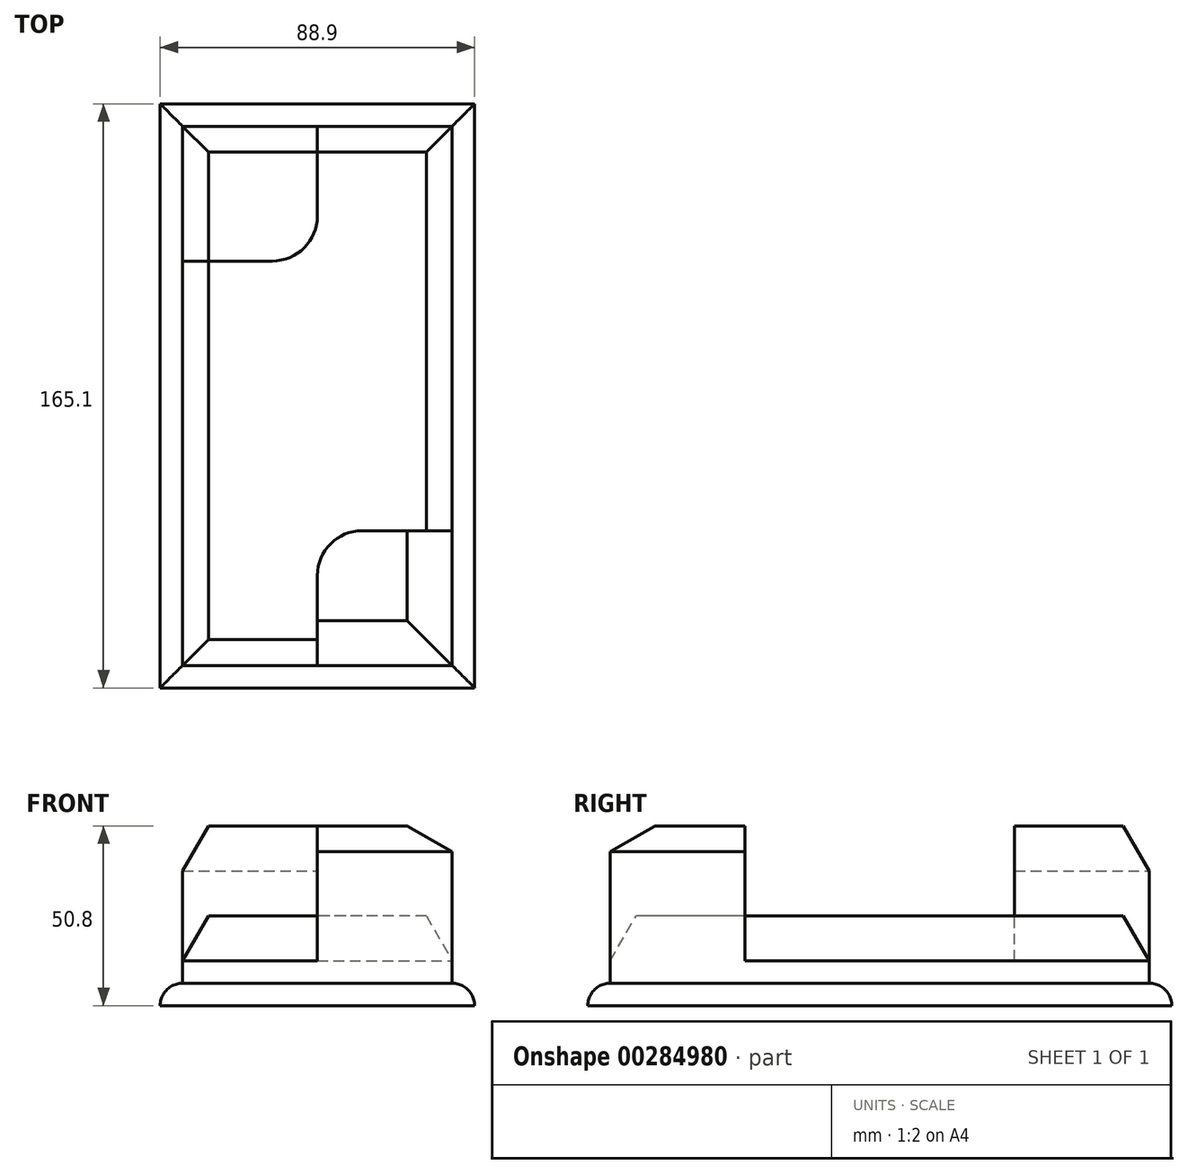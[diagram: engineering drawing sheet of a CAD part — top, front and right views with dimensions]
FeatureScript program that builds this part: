
annotation { "Feature Type Name" : "Feature", "Feature Type Description" : "" }
export const myFeature = defineFeature(function(context is Context, id is Id, definition is map)
    precondition{}
    {
        {
            var Q0;
            Q0=qCreatedBy(makeId("Top.planeOp"),FACE);
            var sketch = newSketch(context, id + "F0", { "sketchPlane" : qUnion([Q0])});
            skLineSegment(sketch, "E0.bottom", {"start": v(38.1, 76.2) * mm, "end": v(-38.1, 76.2) * mm});
            skLineSegment(sketch, "E0.top", {"start": v(38.1, -76.2) * mm, "end": v(-38.1, -76.2) * mm});
            skLineSegment(sketch, "E0.left", {"start": v(38.1, 76.2) * mm, "end": v(38.1, -76.2) * mm});
            skLineSegment(sketch, "E0.right", {"start": v(-38.1, 76.2) * mm, "end": v(-38.1, -76.2) * mm});
            skPoint(sketch, "E0.middle", {"position": v(0, 0) * mm});
            skLineSegment(sketch, "E1.0", {"start": v(44.45, 82.55) * mm, "end": v(-44.45, 82.55) * mm});
            skLineSegment(sketch, "E1.1", {"start": v(44.45, 82.55) * mm, "end": v(44.45, -82.55) * mm});
            skLineSegment(sketch, "E1.2", {"start": v(44.45, -82.55) * mm, "end": v(-44.45, -82.55) * mm});
            skLineSegment(sketch, "E1.3", {"start": v(-44.45, 82.55) * mm, "end": v(-44.45, -82.55) * mm});
            skPoint(sketch, "E2", {"position": v(0, 76.2) * mm});
            skPoint(sketch, "E3", {"position": v(-38.1, 38.1) * mm});
            skLineSegment(sketch, "E4", {"start": v(-38.1, 38.1) * mm, "end": v(-12.7, 38.1) * mm});
            skLineSegment(sketch, "E5", {"start": v(0, 50.8) * mm, "end": v(0, 76.2) * mm});
            skPoint(sketch, "E6.visualSharp", {"position": v(0, 38.1) * mm});
            skArc(sketch, "E6.filletArc", {"start": v(-12.7, 38.1) * mm, "mid": v(-3.72, 41.82) * mm, "end": v(0, 50.8) * mm});
            skPoint(sketch, "E7", {"position": v(38.1, -38.1) * mm});
            skLineSegment(sketch, "E8", {"start": v(38.1, -38.1) * mm, "end": v(38.1, -38.1) * mm});
            skLineSegment(sketch, "E9", {"start": v(0, -76.2) * mm, "end": v(0, -50.8) * mm});
            skLineSegment(sketch, "E10", {"start": v(12.7, -38.1) * mm, "end": v(38.1, -38.1) * mm});
            skPoint(sketch, "E11.visualSharp", {"position": v(0, -38.1) * mm});
            skArc(sketch, "E11.filletArc", {"start": v(12.7, -38.1) * mm, "mid": v(3.72, -41.82) * mm, "end": v(0, -50.8) * mm});
            skSolve(sketch);
        }
        {
            var Q0;
            Q0=makeQuery(id+"F0.imprint","IMPRINT",FACE,{"disambiguationData":[TD([[makeQuery(id+"F0.imprint","IMPRINT",EDGE,{"derivedFrom":sQuery(id+"F0.wireOp",EDGE,"E1.0")}),1.0]])]});
            var Q1;
            {var subQ1=sQuery(id+"F0.wireOp",EDGE,"E4");Q1=makeQuery(id+"F0.imprint","IMPRINT",FACE,{"disambiguationData":[TD([[makeQuery(id+"F0.imprint","IMPRINT",EDGE,{"derivedFrom":subQ1}),1.0]])]});}
            var Q2;
            {var subQ3=sQuery(id+"F0.wireOp",EDGE,"E4");Q2=makeQuery(id+"F0.imprint","IMPRINT",FACE,{"disambiguationData":[TD([[makeQuery(id+"F0.imprint","IMPRINT",EDGE,{"derivedFrom":subQ3}),-1.0]])]});}
            var Q3;
            {var subQ4=sQuery(id+"F0.wireOp",EDGE,"E9");Q3=makeQuery(id+"F0.imprint","IMPRINT",FACE,{"disambiguationData":[TD([[makeQuery(id+"F0.imprint","IMPRINT",EDGE,{"derivedFrom":subQ4}),-1.0]])]});}
            extrude(context, id + "F1", {"entities" : qUnion([Q0, Q1, Q2, Q3]), "depth" : 6.35 * mm});
        }
        {
            var Q0;
            {var subQ3=sQuery(id+"F0.wireOp",EDGE,"E4");Q0=makeQuery(id+"F0.imprint","IMPRINT",FACE,{"disambiguationData":[TD([[makeQuery(id+"F0.imprint","IMPRINT",EDGE,{"derivedFrom":subQ3}),-1.0]])]});}
            var Q1;
            {var subQ1=sQuery(id+"F0.wireOp",EDGE,"E4");Q1=makeQuery(id+"F0.imprint","IMPRINT",FACE,{"disambiguationData":[TD([[makeQuery(id+"F0.imprint","IMPRINT",EDGE,{"derivedFrom":subQ1}),1.0]])]});}
            var Q2;
            {var subQ4=sQuery(id+"F0.wireOp",EDGE,"E9");Q2=makeQuery(id+"F0.imprint","IMPRINT",FACE,{"disambiguationData":[TD([[makeQuery(id+"F0.imprint","IMPRINT",EDGE,{"derivedFrom":subQ4}),-1.0]])]});}
            extrude(context, id + "F2", {"entities" : qUnion([Q0, Q1, Q2]), "operationType" : NewBodyOperationType.ADD, "depth" : 25.4 * mm});
        }
        {
            var Q0;
            {var subQ1=sQuery(id+"F0.wireOp",EDGE,"E4");Q0=makeQuery(id+"F0.imprint","IMPRINT",FACE,{"disambiguationData":[TD([[makeQuery(id+"F0.imprint","IMPRINT",EDGE,{"derivedFrom":subQ1}),1.0]])]});}
            var Q1;
            {var subQ4=sQuery(id+"F0.wireOp",EDGE,"E9");Q1=makeQuery(id+"F0.imprint","IMPRINT",FACE,{"disambiguationData":[TD([[makeQuery(id+"F0.imprint","IMPRINT",EDGE,{"derivedFrom":subQ4}),-1.0]])]});}
            extrude(context, id + "F3", {"entities" : qUnion([Q0, Q1]), "operationType" : NewBodyOperationType.ADD, "depth" : 50.8 * mm});
        }
        {
            var Q0;
            Q0=makeQuery(id+"F2.opExtrude","CAP_EDGE",EDGE,{"disambiguationData":[OSD([sQuery(id+"F0.wireOp",EDGE,"E0.top")])],"isStart":false});
            var Q1;
            Q1=makeQuery(id+"F2.opExtrude","CAP_EDGE",EDGE,{"disambiguationData":[OSD([sQuery(id+"F0.wireOp",EDGE,"E0.right")])],"isStart":false});
            var Q2;
            Q2=makeQuery(id+"F2.opExtrude","CAP_EDGE",EDGE,{"disambiguationData":[OSD([sQuery(id+"F0.wireOp",EDGE,"E0.left")])],"isStart":false});
            var Q3;
            Q3=makeQuery(id+"F2.opExtrude","CAP_EDGE",EDGE,{"disambiguationData":[OSD([sQuery(id+"F0.wireOp",EDGE,"E0.bottom")])],"isStart":false});
            chamfer(context, id + "F4", {"entities" : qUnion([Q0, Q1, Q2, Q3]), "chamferType" : ChamferType.OFFSET_ANGLE, "width" : 12.7 * mm, "oppositeDirection" : false, "angle" : 30 * degree, "tangentPropagation" : true});
        }
        {
            var Q0;
            Q0=makeQuery(id+"F1.opExtrude","CAP_EDGE",EDGE,{"disambiguationData":[OSD([sQuery(id+"F0.wireOp",EDGE,"E1.0")])],"isStart":false});
            var Q1;
            Q1=makeQuery(id+"F1.opExtrude","CAP_EDGE",EDGE,{"disambiguationData":[OSD([sQuery(id+"F0.wireOp",EDGE,"E1.1")])],"isStart":false});
            var Q2;
            Q2=makeQuery(id+"F1.opExtrude","CAP_EDGE",EDGE,{"disambiguationData":[OSD([sQuery(id+"F0.wireOp",EDGE,"E1.3")])],"isStart":false});
            var Q3;
            Q3=makeQuery(id+"F1.opExtrude","CAP_EDGE",EDGE,{"disambiguationData":[OSD([sQuery(id+"F0.wireOp",EDGE,"E1.2")])],"isStart":false});
            fillet(context, id + "F5", {"entities" : qUnion([Q0, Q1, Q2, Q3]), "radius" : 6.35 * mm, "tangentPropagation" : true, "allowEdgeOverflow" : false});
        }
        {
            var Q0;
            Q0=makeQuery(id+"F3.opExtrude","CAP_EDGE",EDGE,{"disambiguationData":[OSD([sQuery(id+"F0.wireOp",EDGE,"E0.right")])],"isStart":false});
            var Q1;
            Q1=makeQuery(id+"F3.opExtrude","CAP_EDGE",EDGE,{"disambiguationData":[OSD([sQuery(id+"F0.wireOp",EDGE,"E0.bottom")])],"isStart":false});
            var Q2;
            Q2=makeQuery(id+"F3.opExtrude","CAP_EDGE",EDGE,{"disambiguationData":[OSD([sQuery(id+"F0.wireOp",EDGE,"E0.top")])],"isStart":false});
            var Q3;
            Q3=makeQuery(id+"F3.opExtrude","CAP_EDGE",EDGE,{"disambiguationData":[OSD([sQuery(id+"F0.wireOp",EDGE,"E0.left")])],"isStart":false});
            chamfer(context, id + "F6", {"entities" : qUnion([Q0, Q1, Q2, Q3]), "chamferType" : ChamferType.OFFSET_ANGLE, "width" : 12.7 * mm, "oppositeDirection" : true, "angle" : 30 * degree, "tangentPropagation" : true});
        }
    });
